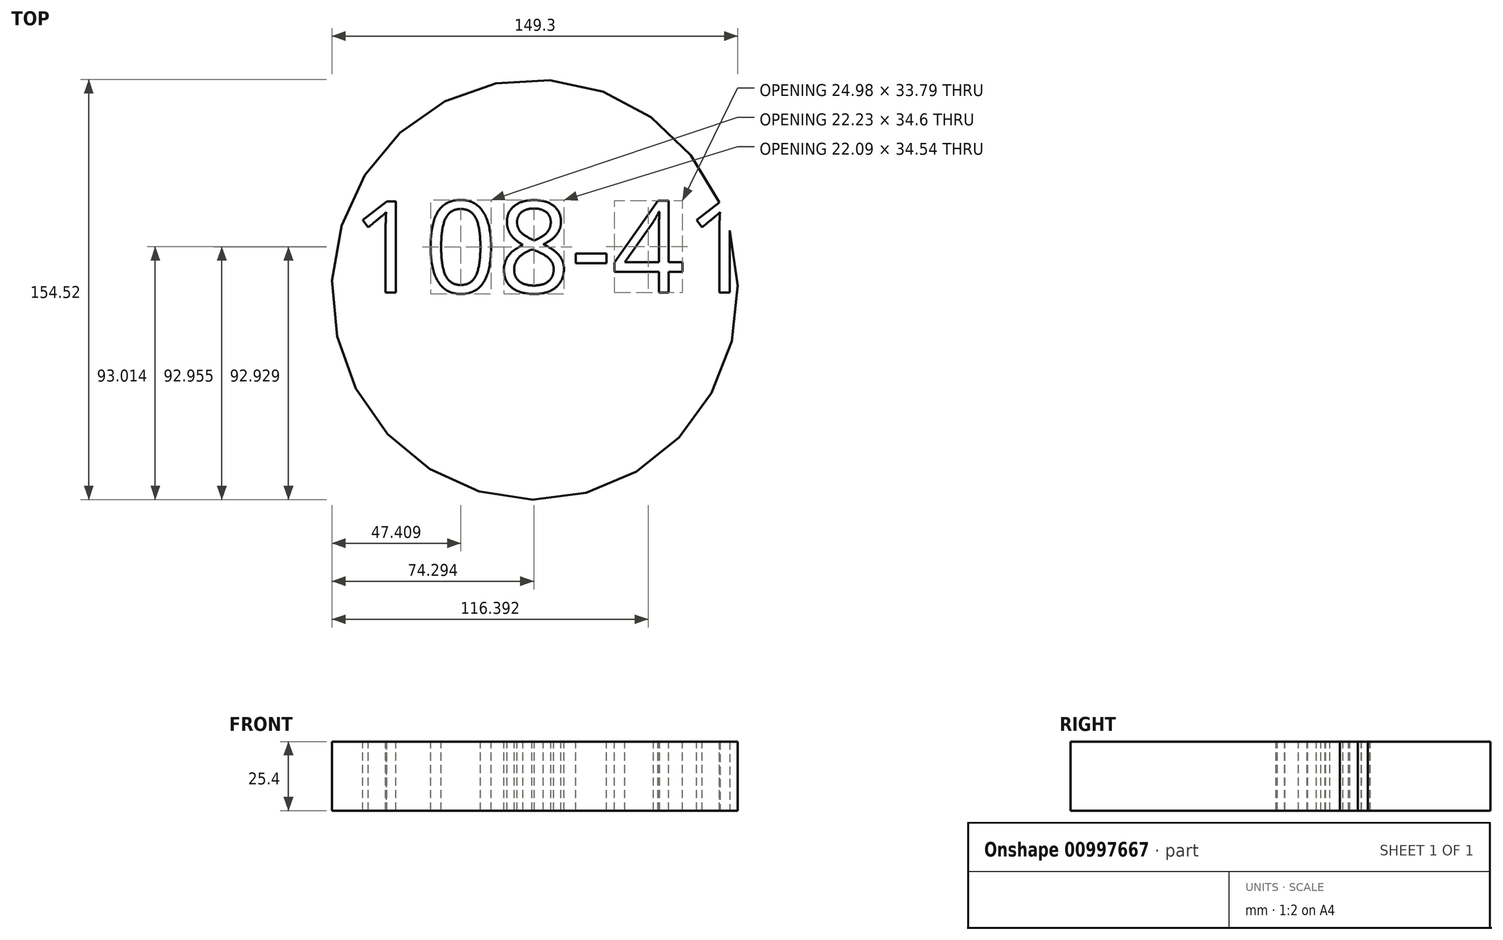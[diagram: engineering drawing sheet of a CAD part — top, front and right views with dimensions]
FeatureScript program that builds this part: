
annotation { "Feature Type Name" : "Feature", "Feature Type Description" : "" }
export const myFeature = defineFeature(function(context is Context, id is Id, definition is map)
    precondition{}
    {
        {
            var Q0;
            Q0=qCreatedBy(makeId("Top.planeOp"),FACE);
            var sketch = newSketch(context, id + "F0", { "sketchPlane" : qUnion([Q0])});
            skEllipse(sketch, "E0", {"center": v(0, 0) * mm, "majorRadius": 74.65 * mm, "minorRadius": 77.26 * mm, "majorAxis": v(1, 0)});
            skSolve(sketch);
        }
        {
            var Q0;
            Q0=makeQuery(id+"F0.imprint","IMPRINT",FACE,{"disambiguationData":[TD([[makeQuery(id+"F0.imprint","IMPRINT",EDGE,{"derivedFrom":sQuery(id+"F0.wireOp",EDGE,"E0")}),1.0]])]});
            extrude(context, id + "F1", {"entities" : qUnion([Q0]), "depth" : 25.4 * mm, "offsetDistance" : 25.4 * mm});
        }
        {
            var Q0;
            Q0=makeQuery(id+"F1.opExtrude","CAP_FACE",FACE,{"disambiguationData":[OSD([sQuery(id+"F0.wireOp",EDGE,"E0")])],"isStart":false});
            var sketch = newSketch(context, id + "F2", { "sketchPlane" : qUnion([Q0])});
            skText(sketch, "E1", { "text": "108-41", "fontName": "OpenSans-Regular.ttf"});
            const initialGuessF2  = {"E1": [-0.06761, -0.00114, 1, 0, 0.03389]};
            skSetInitialGuess(sketch, initialGuessF2);
            skSolve(sketch);
        }
        {
            var Q0;
            Q0 = qSketchRegion(id + "F2", true);
            extrude(context, id + "F3", {"entities" : qUnion([Q0]), "operationType" : NewBodyOperationType.REMOVE, "oppositeDirection" : true, "depth" : 25.4 * mm, "offsetDistance" : 25.4 * mm});
        }
    });
